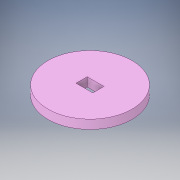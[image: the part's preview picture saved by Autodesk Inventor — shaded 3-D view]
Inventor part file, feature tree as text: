
AUTODESK INVENTOR PART (.ipt)
format: ipt  version: 2019 (Build 230136000, 136)  size: 112,128 bytes
history: native  units: mm
features: other x1, extrude x1, sketch x1
ambient origin geometry x8: Origin, YZ Plane, XZ Plane, XY Plane, X Axis, Y Axis, Z Axis, Center Point
bodies: Body1 (feature_tree)
feature tree (3):
  other  "Sólido1"
  extrude  "Extrusión1"  Depth=4.0mm
  sketch  "Boceto1"  dims[d0=6.0mm d1=4.0mm d2=30.0mm d3=3.18mm d4=0.0mm]
